# Revit family: QF_ELECTROLUXPROFESSIONAL_586619_PBEN20SLCM
name_source: partatom
category: Specialty Equipment
revit_build: Autodesk Revit 2018 (Build: 20190510_1515(x64)
units: mm (PartAtom-declared; Revit-internal decimal feet)

## family parameters
Always vertical = Yes
Cut with Voids When Loaded = No
Part Type = Normal
Room Calculation Point = No
Round Connector Dimension = Use Diameter
Shared = Yes
Work Plane-Based = No

## types (2) — shared parameters
50 Hertz Option = No
60 Hertz Option = Yes
Accessory = Yes
Apparent Power = 0 VA
Base Height = 200 mm  [stored 0.656168 ft]
Compressed Air Pressure = 0.00 psi
Compressed Air Size = 0"
Compressed Air Volume = 0 GPM
Condensate Return Size = 1"
Conn Conduit = Yes
Cycle = 60 Hz
Depth = 900 mm  [stored 2.95276 ft]
Depth Actual = 900 mm  [stored 2.95276 ft]
Direct Waste Size = 0"
Electrical Remarks = 1PH+N 50/60HZ COMPATIBLE
FL Amps = 0 A
Gas Input Pressure = 0.0
Gas Size = 0"
HP = 0.4 HP
Height = 900 mm  [stored 2.95276 ft]
Height Actual = 700 mm  [stored 2.29659 ft]
Indirect Waste Radius Size = 25 mm  [stored 0.082021 ft]
Indirect Waste Size = 2"
Length Actual = 1000 mm  [stored 3.28084 ft]
Max Overcurrent Protection = 5 A
Min Ckt Ampacity = 0 A
Phase = 1
Refrigerant Compressor Remote = Yes
Refrigeration Liquid Line Size = 0"
Refrigeration Suction Line Size = 0"
Steam Consumption per Hour = 100
Steam Supply Size = 1"
URL Cutsheet = www.electrolux.com/foodservice
URL Manufacturer = www.electrolux.com/foodservice
Volts = 230 V
Watts = 0 W
Weight = 150 kg
Width = 1000 mm  [stored 3.28084 ft]
zero-valued in all types: Code, Condensate Return Connection Height, Gas KW, Indirect Waste Connection Height, Steam Supply Connection Height

## per-type parameters (varying)
| type | Cold Water Size | Description | Hot Water Size | Manufacturer | Model | URL |
| 586588_St. BOILING PAN_RECT._80LT (H)_FS | 0" | High Productivity Cooking Steam Rectangular Boiling Pan-80lt Hygienic Profile-Freestanding | 0" | ELECTROLUX | 586588 | www.electrolux.com/foodservice |
| QF_ELECTROLUX_586619_PBEN20SLCM | 1" | STEAM BOILING P+TAP,RECT,200L(H),BS,D900 | 1" | Electrolux | PBEN20SLCM | http://professional.electrolux.com |

note: source unit labels omitted for Gas Input Pressure — the stored unit's dimension contradicts the parameter name (converter mislabeling)

note: [stored X ft] marks values corroborated as IEEE doubles in the binary element streams (Revit-internal decimal feet)

## geometry (parser evidence)
native form markers: Blend x33, Sweep x8
no freeform markers — native parametric forms only
